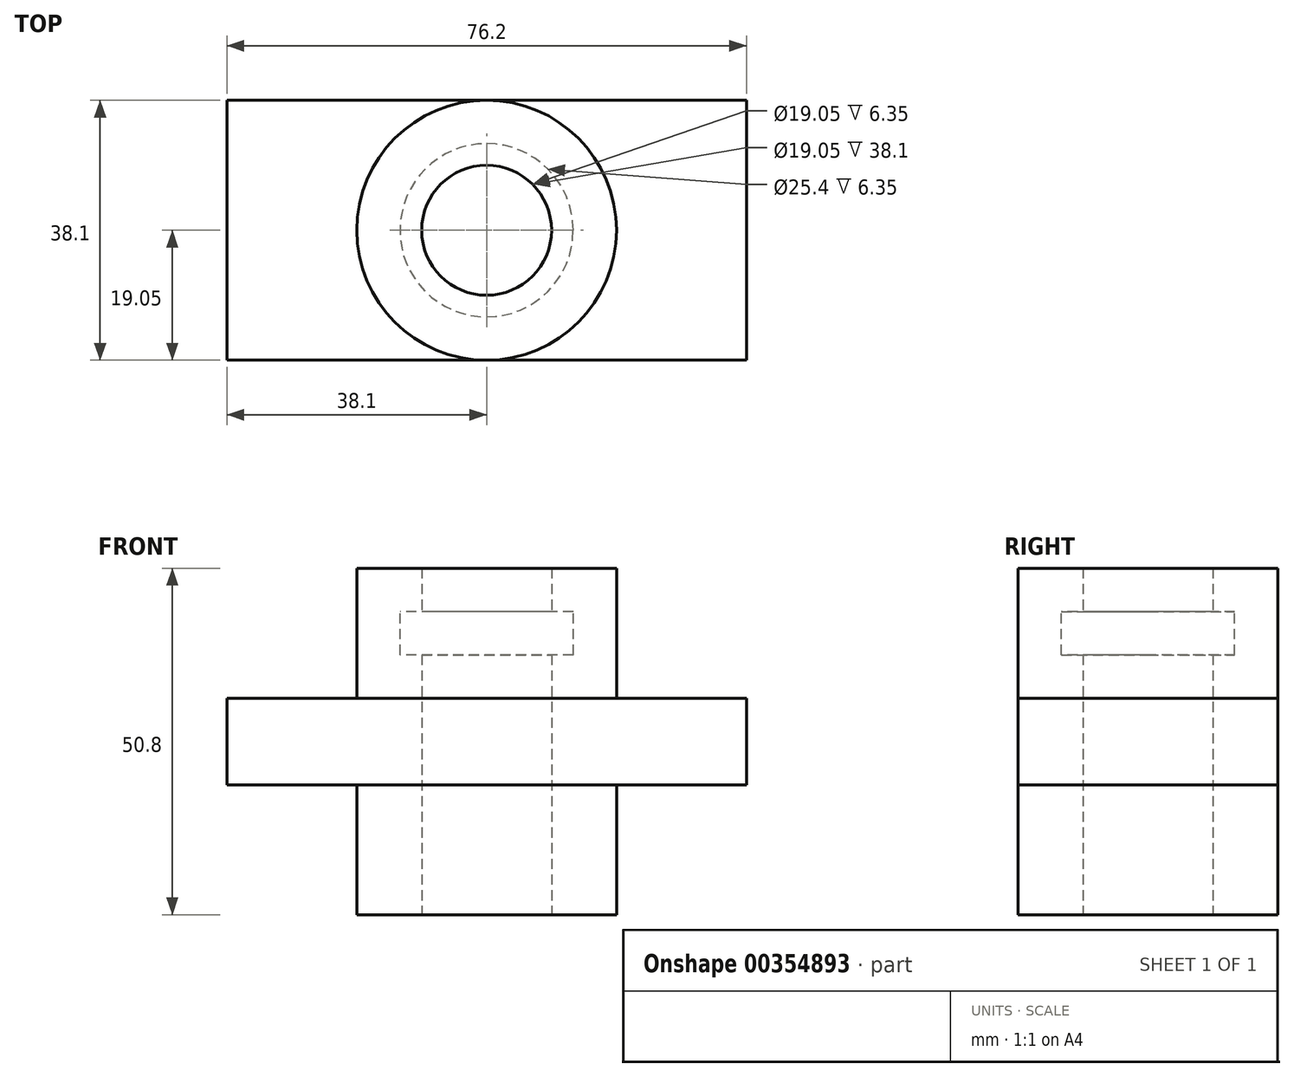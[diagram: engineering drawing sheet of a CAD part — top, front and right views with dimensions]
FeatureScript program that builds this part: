
annotation { "Feature Type Name" : "Feature", "Feature Type Description" : "" }
export const myFeature = defineFeature(function(context is Context, id is Id, definition is map)
    precondition{}
    {
        {
            var Q0;
            Q0=qCreatedBy(makeId("Front.planeOp"),FACE);
            var sketch = newSketch(context, id + "F0", { "sketchPlane" : qUnion([Q0])});
            skLineSegment(sketch, "E0", {"start": v(0, 0) * mm, "end": v(76.2, 0) * mm});
            skLineSegment(sketch, "E1", {"start": v(76.2, 0) * mm, "end": v(76.2, 12.7) * mm});
            skLineSegment(sketch, "E2", {"start": v(76.2, 12.7) * mm, "end": v(0, 12.7) * mm});
            skLineSegment(sketch, "E3", {"start": v(0, 12.7) * mm, "end": v(0, 0) * mm});
            skSolve(sketch);
        }
        {
            var Q0;
            Q0 = qSketchRegion(id + "F0", true);
            extrude(context, id + "F1", {"entities" : qUnion([Q0]), "depth" : 38.1 * mm});
        }
        {
            var Q0;
            Q0=makeQuery(id+"F1.opExtrude","SWEPT_FACE",FACE,{"disambiguationData":[OSD([sQuery(id+"F0.wireOp",EDGE,"E2")])]});
            var sketch = newSketch(context, id + "F2", { "sketchPlane" : qUnion([Q0])});
            skLineSegment(sketch, "E4", {"start": v(38.1, 0) * mm, "end": v(38.1, -38.1) * mm});
            skCircle(sketch, "E5", {"center": v(38.1, -19.05) * mm, "radius": 19.05 * mm});
            skSolve(sketch);
        }
        {
            var Q0;
            Q0 = qSketchRegion(id + "F2", true);
            extrude(context, id + "F3", {"entities" : qUnion([Q0]), "operationType" : NewBodyOperationType.ADD, "depth" : 12.7 * mm});
        }
        {
            var Q0;
            Q0=makeQuery(id+"F3.opExtrude","CAP_FACE",FACE,{"disambiguationData":[OSD([sQuery(id+"F2.wireOp",EDGE,"E5")])],"isStart":false});
            var sketch = newSketch(context, id + "F4", { "sketchPlane" : qUnion([Q0])});
            skCircle(sketch, "E6", {"center": v(38.1, -19.05) * mm, "radius": 12.7 * mm});
            skSolve(sketch);
        }
        {
            var Q0;
            Q0 = qSketchRegion(id + "F4", true);
            extrude(context, id + "F5", {"entities" : qUnion([Q0]), "operationType" : NewBodyOperationType.REMOVE, "oppositeDirection" : true, "depth" : 6.35 * mm});
        }
        {
            var Q0;
            Q0=makeQuery(id+"F3.opExtrude","CAP_FACE",FACE,{"disambiguationData":[OSD([sQuery(id+"F2.wireOp",EDGE,"E5")])],"isStart":false});
            var sketch = newSketch(context, id + "F6", { "sketchPlane" : qUnion([Q0])});
            skCircle(sketch, "E7", {"center": v(38.1, -19.05) * mm, "radius": 19.05 * mm});
            skSolve(sketch);
        }
        {
            var Q0;
            Q0 = qSketchRegion(id + "F6", true);
            extrude(context, id + "F7", {"entities" : qUnion([Q0]), "operationType" : NewBodyOperationType.ADD, "depth" : 6.35 * mm});
        }
        {
            var Q0;
            Q0=makeQuery(id+"F1.opExtrude","SWEPT_FACE",FACE,{"disambiguationData":[OSD([sQuery(id+"F0.wireOp",EDGE,"E0")])]});
            var sketch = newSketch(context, id + "F8", { "sketchPlane" : qUnion([Q0])});
            skLineSegment(sketch, "E8", {"start": v(38.1, 0) * mm, "end": v(38.1, 38.1) * mm});
            skCircle(sketch, "E9", {"center": v(38.1, 19.05) * mm, "radius": 19.05 * mm});
            skSolve(sketch);
        }
        {
            var Q0;
            Q0 = qSketchRegion(id + "F8", true);
            extrude(context, id + "F9", {"entities" : qUnion([Q0]), "operationType" : NewBodyOperationType.ADD, "depth" : 19.05 * mm});
        }
        {
            var Q0;
            Q0=makeQuery(id+"F9.opExtrude","CAP_FACE",FACE,{"disambiguationData":[OSD([sQuery(id+"F8.wireOp",EDGE,"E9")])],"isStart":false});
            var sketch = newSketch(context, id + "F10", { "sketchPlane" : qUnion([Q0])});
            skCircle(sketch, "E10", {"center": v(38.1, 19.05) * mm, "radius": 9.53 * mm});
            skSolve(sketch);
        }
        {
            var Q0;
            Q0 = qSketchRegion(id + "F10", true);
            extrude(context, id + "F11", {"entities" : qUnion([Q0]), "operationType" : NewBodyOperationType.REMOVE, "oppositeDirection" : true, "depth" : 152.4 * mm});
        }
    });
